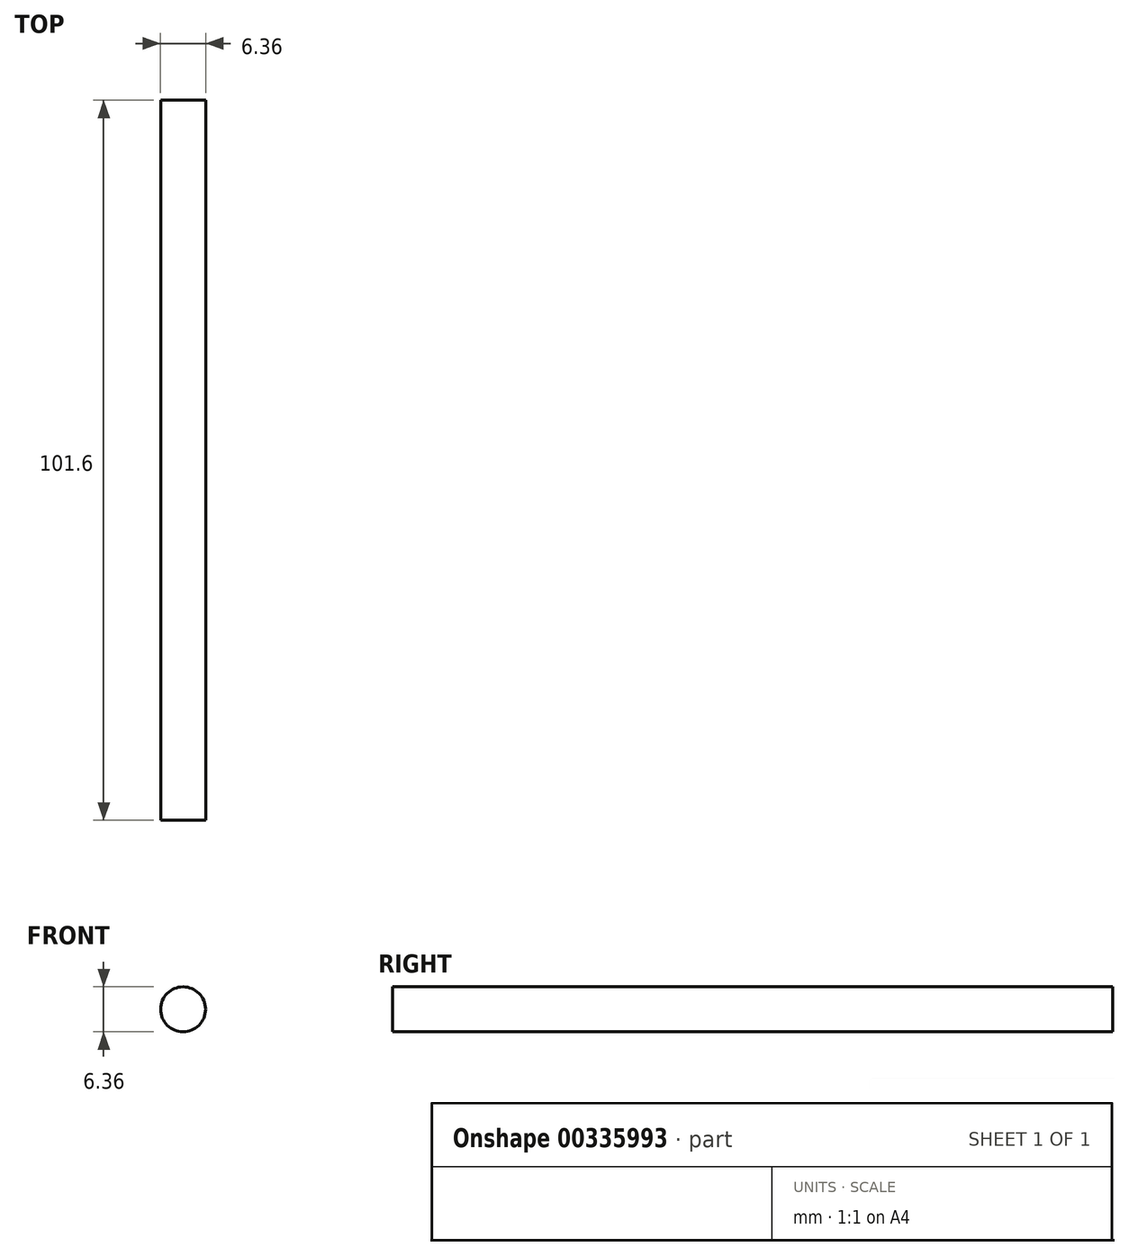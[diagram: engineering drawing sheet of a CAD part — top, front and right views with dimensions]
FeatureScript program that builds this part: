
annotation { "Feature Type Name" : "Feature", "Feature Type Description" : "" }
export const myFeature = defineFeature(function(context is Context, id is Id, definition is map)
    precondition{}
    {
        {
            var Q0;
            Q0=qCreatedBy(makeId("Front.planeOp"),FACE);
            var sketch = newSketch(context, id + "F0", { "sketchPlane" : qUnion([Q0])});
            skCircle(sketch, "E0", {"center": v(0, 0) * mm, "radius": 3.18 * mm});
            skSolve(sketch);
        }
        {
            var Q0;
            Q0=makeQuery(id+"F0.imprint","IMPRINT",FACE,{"disambiguationData":[TD([[makeQuery(id+"F0.imprint","IMPRINT",EDGE,{"derivedFrom":sQuery(id+"F0.wireOp",EDGE,"E0")}),1.0]])]});
            extrude(context, id + "F1", {"entities" : qUnion([Q0]), "endBound" : BoundingType.SYMMETRIC, "depth" : 101.6 * mm});
        }
    });
